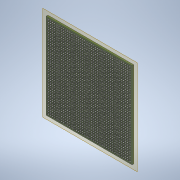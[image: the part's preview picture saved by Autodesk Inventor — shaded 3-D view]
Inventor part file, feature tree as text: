
AUTODESK INVENTOR PART (.ipt)
format: ipt  version: 2021 (Build 250183000, 183)  size: 6,204,928 bytes
history: native  units: in
note: dims shown in document units (in); Inventor stores cm internally (conversion verified against a paired STEP export)
features: extrude x3, sketch x3, pattern_linear x2, plane x1, mirror x1
ambient origin geometry x8: Origin, YZ Plane, XZ Plane, XY Plane, X Axis, Y Axis, Z Axis, Center Point
bodies: Solid1 (feature_tree)
feature tree (10):
  extrude  "Extrusion1"  Depth=2.0in
  extrude  "Extrusion2"  Depth=0.0394in
  pattern_linear  "Rectangular Pattern1"  Spacing1=0.05in  [1 undecoded]
  extrude  "Extrusion3"  TaperAngle=0.0deg  [1 undecoded]
  pattern_linear  "Rectangular Pattern2"  Count1=39 Spacing1=0.05in
  plane  "Work Plane1"
  mirror  "Mirror1"
  sketch  "Sketch1"  dims[d0=2.0in d1=2.0in]
  sketch  "Sketch2"  dims[d2=0.0394in d3=0.0in d4=0.0256in]
  sketch  "Sketch3"  dims[d5=0.05in d6=0.05in d7=0.0in d8=0.0in d9=15.3543in d11=0.05in d12=15.3543in d14=0.05in d15=0.0394in d16=0.0006in d17=0.0in d18=15.3543in d20=0.05in d21=15.3543in d23=0.05in]
note: 2 required parameter values undecoded (feature->parameter linkage not recoverable at this tier; creation-order binding heuristic only, values carry confidence <= 0.55)
